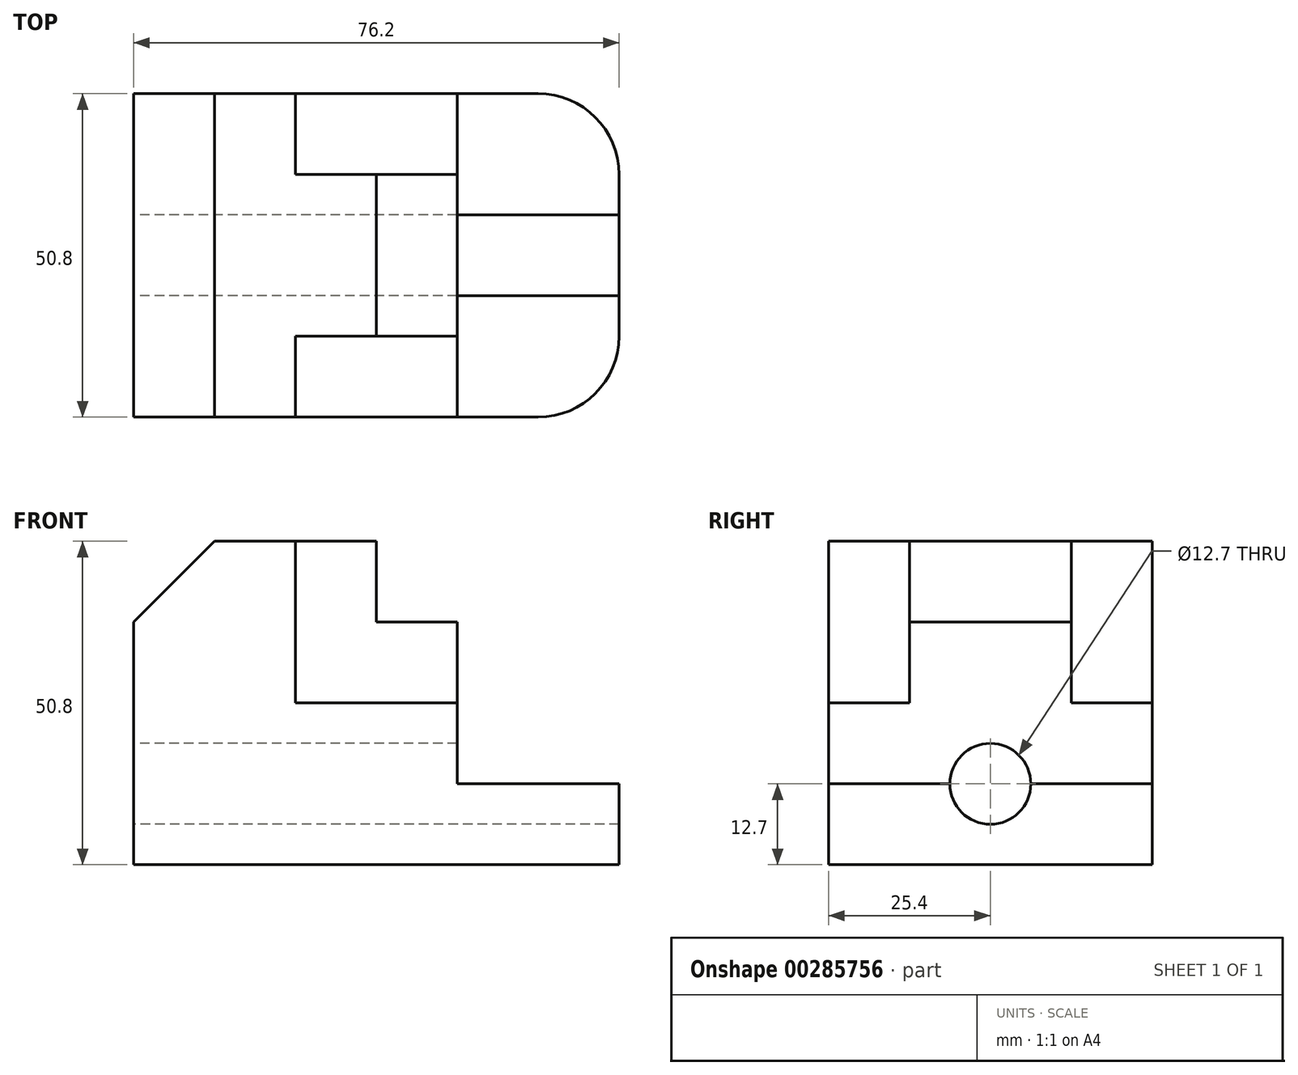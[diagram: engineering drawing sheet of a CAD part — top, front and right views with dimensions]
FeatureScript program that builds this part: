
annotation { "Feature Type Name" : "Feature", "Feature Type Description" : "" }
export const myFeature = defineFeature(function(context is Context, id is Id, definition is map)
    precondition{}
    {
        {
            var Q0;
            Q0=qCreatedBy(makeId("Top.planeOp"),FACE);
            var sketch = newSketch(context, id + "F0", { "sketchPlane" : qUnion([Q0])});
            skLineSegment(sketch, "E0", {"start": v(0, 25.4) * mm, "end": v(0, -25.4) * mm});
            skLineSegment(sketch, "E1", {"start": v(0, -25.4) * mm, "end": v(63.5, -25.4) * mm});
            skLineSegment(sketch, "E2", {"start": v(63.5, -25.4) * mm, "end": v(63.5, 25.4) * mm});
            skLineSegment(sketch, "E3", {"start": v(63.5, 25.4) * mm, "end": v(0, 25.4) * mm});
            skLineSegment(sketch, "E4", {"start": v(76.2, 12.7) * mm, "end": v(76.2, -12.7) * mm});
            skArc(sketch, "E5", {"start": v(76.2, 12.7) * mm, "mid": v(72.48, 21.68) * mm, "end": v(63.5, 25.4) * mm});
            skArc(sketch, "E6", {"start": v(76.2, -12.7) * mm, "mid": v(72.48, -21.68) * mm, "end": v(63.5, -25.4) * mm});
            skSolve(sketch);
        }
        {
            var Q0;
            Q0 = qSketchRegion(id + "F0", true);
            extrude(context, id + "F1", {"entities" : qUnion([Q0]), "oppositeDirection" : true, "depth" : 50.8 * mm});
        }
        {
            var Q0;
            Q0=qCreatedBy(makeId("Front.planeOp"),FACE);
            var sketch = newSketch(context, id + "F2", { "sketchPlane" : qUnion([Q0])});
            skLineSegment(sketch, "E7", {"start": v(0, 0) * mm, "end": v(12.7, 0) * mm});
            skLineSegment(sketch, "E8", {"start": v(0, 0) * mm, "end": v(0, -12.7) * mm});
            skLineSegment(sketch, "E9", {"start": v(0, -12.7) * mm, "end": v(12.7, 0) * mm});
            skSolve(sketch);
        }
        {
            var Q0;
            Q0 = qSketchRegion(id + "F2", true);
            extrude(context, id + "F3", {"entities" : qUnion([Q0]), "operationType" : NewBodyOperationType.REMOVE, "endBound" : BoundingType.SYMMETRIC, "oppositeDirection" : true, "depth" : 25400 * mm});
        }
        {
            var Q0;
            Q0=qCreatedBy(makeId("Top.planeOp"),FACE);
            var sketch = newSketch(context, id + "F4", { "sketchPlane" : qUnion([Q0])});
            skLineSegment(sketch, "E10", {"start": v(50.8, 25.4) * mm, "end": v(76.2, 25.4) * mm});
            skLineSegment(sketch, "E11", {"start": v(76.2, 25.4) * mm, "end": v(76.2, -25.4) * mm});
            skLineSegment(sketch, "E12", {"start": v(76.2, -25.4) * mm, "end": v(50.8, -25.4) * mm});
            skLineSegment(sketch, "E13", {"start": v(50.8, 25.4) * mm, "end": v(50.8, -25.4) * mm});
            skSolve(sketch);
        }
        {
            var Q0;
            Q0 = qSketchRegion(id + "F4", true);
            extrude(context, id + "F5", {"entities" : qUnion([Q0]), "operationType" : NewBodyOperationType.REMOVE, "oppositeDirection" : true, "depth" : 38.1 * mm});
        }
        {
            var Q0;
            Q0=qCreatedBy(makeId("Top.planeOp"),FACE);
            var sketch = newSketch(context, id + "F6", { "sketchPlane" : qUnion([Q0])});
            skLineSegment(sketch, "E14.bottom", {"start": v(50.8, 25.4) * mm, "end": v(25.4, 25.4) * mm});
            skLineSegment(sketch, "E14.top", {"start": v(50.8, 12.7) * mm, "end": v(25.4, 12.7) * mm});
            skLineSegment(sketch, "E14.left", {"start": v(50.8, 25.4) * mm, "end": v(50.8, 12.7) * mm});
            skLineSegment(sketch, "E14.right", {"start": v(25.4, 25.4) * mm, "end": v(25.4, 12.7) * mm});
            skSolve(sketch);
        }
        {
            var Q0;
            Q0 = qSketchRegion(id + "F6", true);
            extrude(context, id + "F7", {"entities" : qUnion([Q0]), "operationType" : NewBodyOperationType.REMOVE, "oppositeDirection" : true, "depth" : 25.4 * mm});
        }
        {
            var Q0;
            Q0=qCreatedBy(makeId("Top.planeOp"),FACE);
            var sketch = newSketch(context, id + "F8", { "sketchPlane" : qUnion([Q0])});
            skLineSegment(sketch, "E15.bottom", {"start": v(50.8, -25.4) * mm, "end": v(25.4, -25.4) * mm});
            skLineSegment(sketch, "E15.top", {"start": v(50.8, -12.7) * mm, "end": v(25.4, -12.7) * mm});
            skLineSegment(sketch, "E15.left", {"start": v(50.8, -25.4) * mm, "end": v(50.8, -12.7) * mm});
            skLineSegment(sketch, "E15.right", {"start": v(25.4, -25.4) * mm, "end": v(25.4, -12.7) * mm});
            skSolve(sketch);
        }
        {
            var Q0;
            Q0 = qSketchRegion(id + "F8", true);
            extrude(context, id + "F9", {"entities" : qUnion([Q0]), "operationType" : NewBodyOperationType.REMOVE, "oppositeDirection" : true, "depth" : 25.4 * mm});
        }
        {
            var Q0;
            Q0=qCreatedBy(makeId("Top.planeOp"),FACE);
            var sketch = newSketch(context, id + "F10", { "sketchPlane" : qUnion([Q0])});
            skLineSegment(sketch, "E16.bottom", {"start": v(38.1, 12.7) * mm, "end": v(50.8, 12.7) * mm});
            skLineSegment(sketch, "E16.top", {"start": v(38.1, -12.7) * mm, "end": v(50.8, -12.7) * mm});
            skLineSegment(sketch, "E16.left", {"start": v(38.1, 12.7) * mm, "end": v(38.1, -12.7) * mm});
            skLineSegment(sketch, "E16.right", {"start": v(50.8, 12.7) * mm, "end": v(50.8, -12.7) * mm});
            skSolve(sketch);
        }
        {
            var Q0;
            Q0 = qSketchRegion(id + "F10", true);
            extrude(context, id + "F11", {"entities" : qUnion([Q0]), "operationType" : NewBodyOperationType.REMOVE, "oppositeDirection" : true, "depth" : 12.7 * mm});
        }
        {
            var Q0;
            Q0=qCreatedBy(makeId("Right.planeOp"),FACE);
            var sketch = newSketch(context, id + "F12", { "sketchPlane" : qUnion([Q0])});
            skCircle(sketch, "E17", {"center": v(0, -38.1) * mm, "radius": 6.35 * mm});
            skSolve(sketch);
        }
        {
            var Q0;
            Q0 = qSketchRegion(id + "F12", true);
            extrude(context, id + "F13", {"entities" : qUnion([Q0]), "operationType" : NewBodyOperationType.REMOVE, "depth" : 107.7 * mm});
        }
    });
